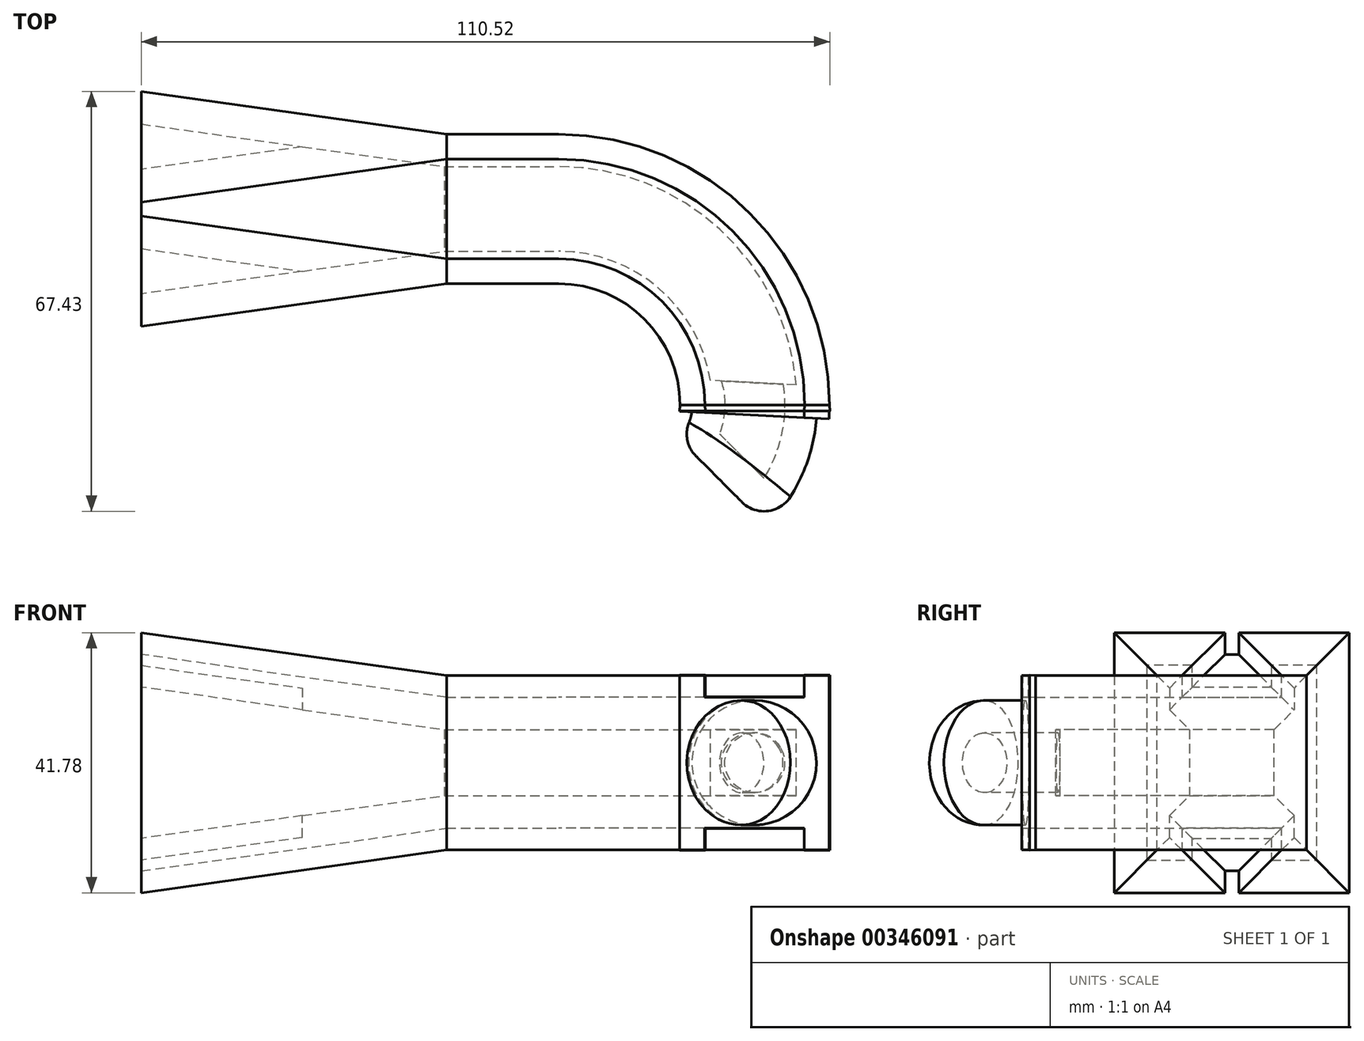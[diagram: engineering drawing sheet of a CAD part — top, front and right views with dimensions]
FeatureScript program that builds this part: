
annotation { "Feature Type Name" : "Feature", "Feature Type Description" : "" }
export const myFeature = defineFeature(function(context is Context, id is Id, definition is map)
    precondition{}
    {
        {
            var Q0;
            Q0=qCreatedBy(makeId("Front.planeOp"),FACE);
            var sketch = newSketch(context, id + "F0", { "sketchPlane" : qUnion([Q0])});
            skCircle(sketch, "E0", {"center": v(0, 0) * mm, "radius": 10 * mm});
            skSolve(sketch);
        }
        {
            var Q0;
            Q0=qCreatedBy(makeId("Front.planeOp"),FACE);
            var sketch = newSketch(context, id + "F1", { "sketchPlane" : qUnion([Q0])});
            skLineSegment(sketch, "E1", {"start": v(-17.65, 8.88) * mm, "end": v(-17.65, -11.04) * mm});
            skSolve(sketch);
        }
        {
            var Q0;
            Q0=makeQuery(id+"F0.imprint","IMPRINT",FACE,{"disambiguationData":[TD([[makeQuery(id+"F0.imprint","IMPRINT",EDGE,{"derivedFrom":sQuery(id+"F0.wireOp",EDGE,"E0")}),1.0]])]});
            var Q1;
            Q1=sQuery(id+"F1.wireOp",EDGE,"E1");
            revolve(context, id + "F2", {"entities" : qUnion([Q0]), "axis" : qUnion([Q1]), "revolveType" : RevolveType.ONE_DIRECTION, "angle" : 45 * degree});
        }
        {
            var Q0;
            Q0=qCreatedBy(makeId("Front.planeOp"),FACE);
            var sketch = newSketch(context, id + "F3", { "sketchPlane" : qUnion([Q0])});
            skLineSegment(sketch, "E2.bottom", {"start": v(10, -10.5) * mm, "end": v(-10, -10.5) * mm});
            skLineSegment(sketch, "E2.top", {"start": v(10, 10.5) * mm, "end": v(-10, 10.5) * mm});
            skLineSegment(sketch, "E2.left", {"start": v(10, -10.5) * mm, "end": v(10, 10.5) * mm});
            skLineSegment(sketch, "E2.right", {"start": v(-10, -10.5) * mm, "end": v(-10, 10.5) * mm});
            skPoint(sketch, "E2.middle", {"position": v(0, 0) * mm});
            skLineSegment(sketch, "E3.bottom", {"start": v(-8, 14) * mm, "end": v(-12, 14) * mm});
            skLineSegment(sketch, "E3.top", {"start": v(-8, -14) * mm, "end": v(-12, -14) * mm});
            skLineSegment(sketch, "E3.left", {"start": v(-8, 14) * mm, "end": v(-8, -14) * mm});
            skLineSegment(sketch, "E3.right", {"start": v(-12, 14) * mm, "end": v(-12, -14) * mm});
            skPoint(sketch, "E3.middle", {"position": v(-10, 0) * mm});
            skLineSegment(sketch, "E4.bottom", {"start": v(8, 14) * mm, "end": v(12, 14) * mm});
            skLineSegment(sketch, "E4.top", {"start": v(8, -14) * mm, "end": v(12, -14) * mm});
            skLineSegment(sketch, "E4.left", {"start": v(8, 14) * mm, "end": v(8, -14) * mm});
            skLineSegment(sketch, "E4.right", {"start": v(12, 14) * mm, "end": v(12, -14) * mm});
            skPoint(sketch, "E4.middle", {"position": v(10, 0) * mm});
            skSolve(sketch);
        }
        {
            var Q0;
            Q0=qCreatedBy(makeId("Front.planeOp"),FACE);
            var sketch = newSketch(context, id + "F4", { "sketchPlane" : qUnion([Q0])});
            skLineSegment(sketch, "E5", {"start": v(-31.47, -8.83) * mm, "end": v(-31.47, 9.58) * mm});
            skSolve(sketch);
        }
        {
            var Q0;
            {var subQ1=sQuery(id+"F3.wireOp",EDGE,"E2.right");Q0=makeQuery(id+"F3.imprint","IMPRINT",FACE,{"disambiguationData":[TD([[makeQuery(id+"F3.imprint","IMPRINT",EDGE,{"derivedFrom":subQ1}),1.0]])]});}
            var Q1;
            {var subQ0=sQuery(id+"F3.wireOp",EDGE,"E4.left");var subQ1=sQuery(id+"F3.wireOp",EDGE,"E2.bottom");var subQ2=makeQuery(id+"F3.imprint","INTERSECT",VERTEX,{"derivedFrom":[subQ1,subQ0]});Q1=makeQuery(id+"F3.imprint","IMPRINT",FACE,{"disambiguationData":[TD([[makeQuery(id+"F3.imprint","IMPRINT",EDGE,{"disambiguationData":[TD([[subQ2,-1.0]])],"derivedFrom":subQ1}),-1.0]])]});}
            var Q2;
            {var subQ1=sQuery(id+"F3.wireOp",EDGE,"E2.left");Q2=makeQuery(id+"F3.imprint","IMPRINT",FACE,{"disambiguationData":[TD([[makeQuery(id+"F3.imprint","IMPRINT",EDGE,{"derivedFrom":subQ1}),-1.0]])]});}
            var Q3;
            {var subQ0=sQuery(id+"F3.wireOp",EDGE,"E2.left");Q3=makeQuery(id+"F3.imprint","IMPRINT",FACE,{"disambiguationData":[TD([[makeQuery(id+"F3.imprint","IMPRINT",EDGE,{"derivedFrom":subQ0}),1.0]])]});}
            var Q4;
            {var subQ0=sQuery(id+"F3.wireOp",EDGE,"E2.right");Q4=makeQuery(id+"F3.imprint","IMPRINT",FACE,{"disambiguationData":[TD([[makeQuery(id+"F3.imprint","IMPRINT",EDGE,{"derivedFrom":subQ0}),-1.0]])]});}
            extrude(context, id + "F5", {"entities" : qUnion([Q0, Q1, Q2, Q3, Q4]), "operationType" : NewBodyOperationType.ADD, "depth" : 1 * mm, "hasDraft" : true, "draftAngle" : 3 * degree});
        }
        {
            var Q0;
            Q0=makeQuery(id+"F5.boolean.opBoolean","MERGE",FACE,{"derivedFrom":[makeQuery(id+"F2.opRevolve","CAP_FACE",FACE,{"disambiguationData":[OSD([sQuery(id+"F0.wireOp",EDGE,"E0")])],"isStart":true}),makeQuery(id+"F5.opExtrude","CAP_FACE",FACE,{"disambiguationData":[OSD([sQuery(id+"F3.wireOp",EDGE,"E2.bottom"),sQuery(id+"F3.wireOp",EDGE,"E2.top"),sQuery(id+"F3.wireOp",EDGE,"E3.bottom"),sQuery(id+"F3.wireOp",EDGE,"E3.top"),sQuery(id+"F3.wireOp",EDGE,"E3.left"),sQuery(id+"F3.wireOp",EDGE,"E3.right"),sQuery(id+"F3.wireOp",EDGE,"E4.bottom"),sQuery(id+"F3.wireOp",EDGE,"E4.top"),sQuery(id+"F3.wireOp",EDGE,"E4.left"),sQuery(id+"F3.wireOp",EDGE,"E4.right")])],"isStart":true})]});
            var Q1;
            Q1=sQuery(id+"F4.wireOp",EDGE,"E5");
            revolve(context, id + "F6", {"operationType" : NewBodyOperationType.ADD, "entities" : qUnion([Q0]), "axis" : qUnion([Q1]), "revolveType" : RevolveType.TWO_DIRECTIONS, "oppositeDirection" : true, "angle" : 3 * degree, "angleBack" : 270 * degree});
        }
        {
            var Q0;
            Q0=makeQuery(id+"F6.opRevolve","CAP_FACE",FACE,{"disambiguationData":[OSD([sQuery(id+"F0.wireOp",EDGE,"E0"),sQuery(id+"F3.wireOp",EDGE,"E2.bottom"),sQuery(id+"F3.wireOp",EDGE,"E2.top"),sQuery(id+"F3.wireOp",EDGE,"E3.bottom"),sQuery(id+"F3.wireOp",EDGE,"E3.top"),sQuery(id+"F3.wireOp",EDGE,"E3.left"),sQuery(id+"F3.wireOp",EDGE,"E3.right"),sQuery(id+"F3.wireOp",EDGE,"E4.bottom"),sQuery(id+"F3.wireOp",EDGE,"E4.top"),sQuery(id+"F3.wireOp",EDGE,"E4.left"),sQuery(id+"F3.wireOp",EDGE,"E4.right")])],"isStart":true});
            var sketch = newSketch(context, id + "F7", { "sketchPlane" : qUnion([Q0])});
            skLineSegment(sketch, "E6", {"start": v(-77.27, 19.39) * mm, "end": v(-77.27, -18.68) * mm});
            skSolve(sketch);
        }
        {
            var Q0;
            {var subQ6=sQuery(id+"F3.wireOp",EDGE,"E2.bottom");Q0=makeQuery(id+"F7.imprint","IMPRINT",FACE,{"disambiguationData":[TD([[makeQuery(id+"F7.imprint","IMPRINT",EDGE,{"derivedFrom":makeQuery(id+"F6.opRevolve","CAP_EDGE",EDGE,{"disambiguationData":[OSD([subQ6])],"isStart":true})}),1.0]])]});}
            extrude(context, id + "F8", {"entities" : qUnion([Q0]), "operationType" : NewBodyOperationType.ADD, "depth" : 18 * mm});
        }
        {
            var Q0;
            Q0=makeQuery(id+"F8.opExtrude","CAP_FACE",FACE,{"disambiguationData":[OSD([sQuery(id+"F3.wireOp",EDGE,"E2.bottom"),sQuery(id+"F3.wireOp",EDGE,"E2.top"),sQuery(id+"F3.wireOp",EDGE,"E3.bottom"),sQuery(id+"F3.wireOp",EDGE,"E3.top"),sQuery(id+"F3.wireOp",EDGE,"E3.left"),sQuery(id+"F3.wireOp",EDGE,"E3.right"),sQuery(id+"F3.wireOp",EDGE,"E4.bottom"),sQuery(id+"F3.wireOp",EDGE,"E4.top"),sQuery(id+"F3.wireOp",EDGE,"E4.left"),sQuery(id+"F3.wireOp",EDGE,"E4.right")])],"isStart":false});
            extrude(context, id + "F9", {"entities" : qUnion([Q0]), "operationType" : NewBodyOperationType.ADD, "depth" : 49 * mm, "hasDraft" : true, "draftAngle" : 8 * degree});
        }
        {
            var Q0;
            Q0=makeQuery(id+"F9.opExtrude","CAP_FACE",FACE,{"disambiguationData":[OSD([sQuery(id+"F3.wireOp",EDGE,"E2.bottom"),sQuery(id+"F3.wireOp",EDGE,"E2.top"),sQuery(id+"F3.wireOp",EDGE,"E3.bottom"),sQuery(id+"F3.wireOp",EDGE,"E3.top"),sQuery(id+"F3.wireOp",EDGE,"E3.left"),sQuery(id+"F3.wireOp",EDGE,"E3.right"),sQuery(id+"F3.wireOp",EDGE,"E4.bottom"),sQuery(id+"F3.wireOp",EDGE,"E4.top"),sQuery(id+"F3.wireOp",EDGE,"E4.left"),sQuery(id+"F3.wireOp",EDGE,"E4.right")])],"isStart":false});
            shell(context, id + "F10", {"entities" : qUnion([Q0]), "thickness" : 5.2 * mm});
        }
        {
            var Q0;
            Q0=makeQuery(id+"F2.opRevolve","CAP_EDGE",EDGE,{"disambiguationData":[OSD([sQuery(id+"F0.wireOp",EDGE,"E0")])],"isStart":false});
            fillet(context, id + "F11", {"entities" : qUnion([Q0]), "radius" : 5 * mm, "tangentPropagation" : true, "allowEdgeOverflow" : false});
        }
    });
